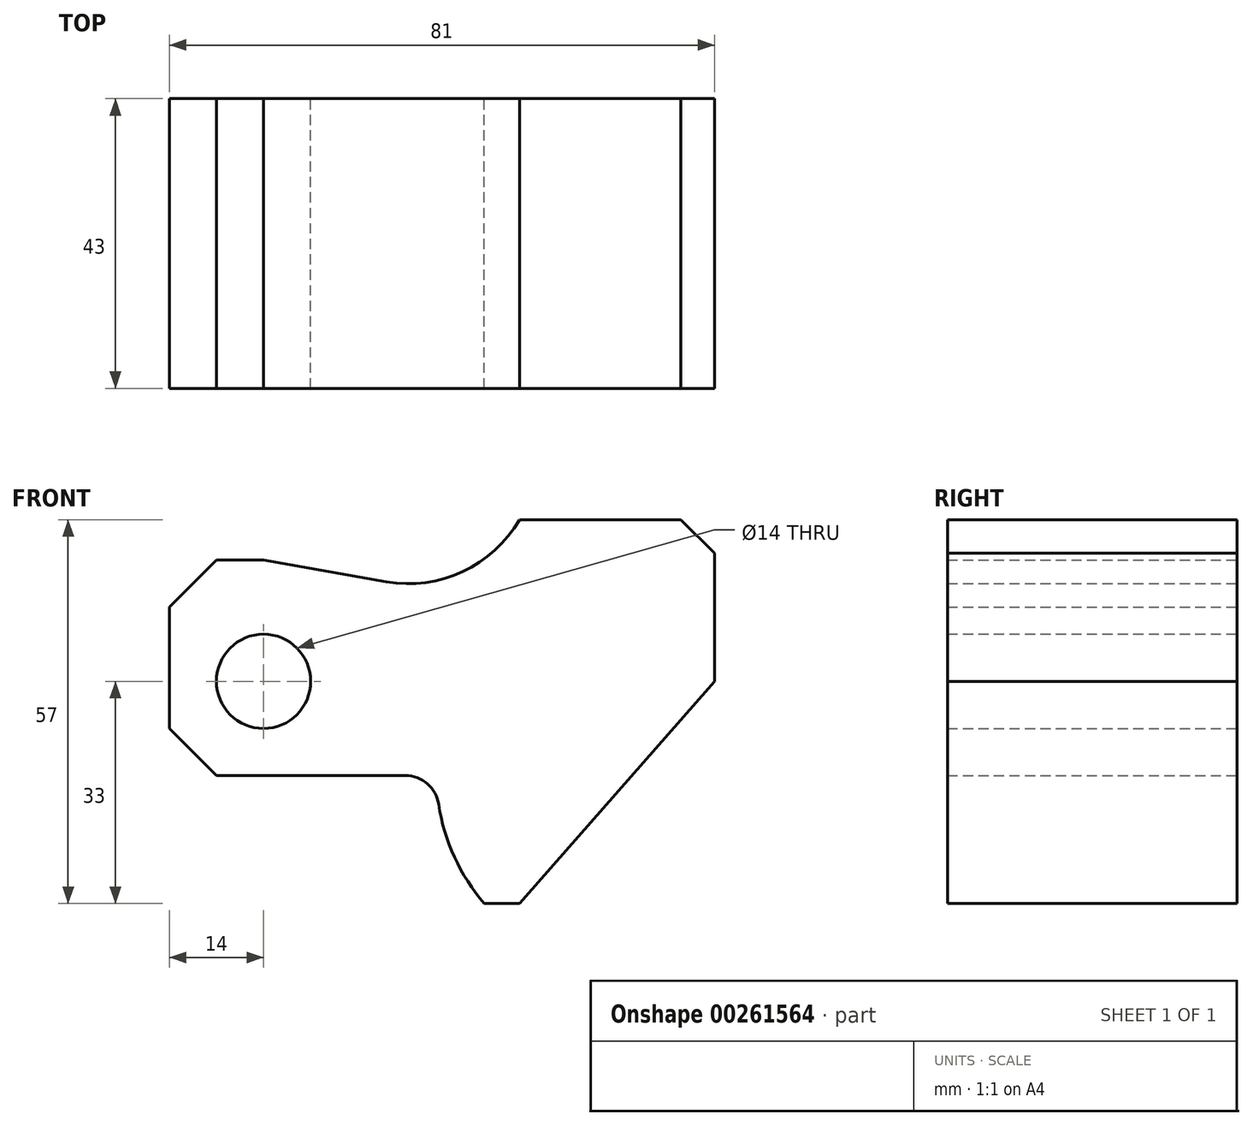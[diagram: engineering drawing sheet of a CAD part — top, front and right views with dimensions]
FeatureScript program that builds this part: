
annotation { "Feature Type Name" : "Feature", "Feature Type Description" : "" }
export const myFeature = defineFeature(function(context is Context, id is Id, definition is map)
    precondition{}
    {
        {
            var Q0;
            Q0=qCreatedBy(makeId("Front.planeOp"),FACE);
            var sketch = newSketch(context, id + "F0", { "sketchPlane" : qUnion([Q0])});
            skCircle(sketch, "E0", {"center": v(0, 0) * mm, "radius": 7 * mm});
            skLineSegment(sketch, "E1", {"start": v(-7, -14) * mm, "end": v(21.07, -14) * mm});
            skLineSegment(sketch, "E2", {"start": v(-7, -14) * mm, "end": v(-14, -7) * mm});
            skLineSegment(sketch, "E3", {"start": v(-14, -7) * mm, "end": v(-14, 11) * mm});
            skLineSegment(sketch, "E4", {"start": v(-14, 11) * mm, "end": v(-7, 18) * mm});
            skLineSegment(sketch, "E5", {"start": v(-7, 18) * mm, "end": v(0, 18) * mm});
            skLineSegment(sketch, "E6", {"start": v(0, 18) * mm, "end": v(18.24, 14.78) * mm});
            skLineSegment(sketch, "E7", {"start": v(67, 0) * mm, "end": v(67, 19) * mm});
            skLineSegment(sketch, "E8", {"start": v(32.79, -33) * mm, "end": v(38, -33) * mm});
            skLineSegment(sketch, "E9", {"start": v(38, -33) * mm, "end": v(67, 0) * mm});
            skLineSegment(sketch, "E10", {"start": v(67, 19) * mm, "end": v(62, 24) * mm});
            skLineSegment(sketch, "E11", {"start": v(62, 24) * mm, "end": v(38, 24) * mm});
            skArc(sketch, "E12", {"start": v(18.24, 14.78) * mm, "mid": v(29.57, 16.28) * mm, "end": v(38, 24) * mm});
            skLineSegment(sketch, "E13", {"start": v(21.07, -14) * mm, "end": v(54.7, -14) * mm, "construction": true});
            skArc(sketch, "E14", {"start": v(26.01, -18.26) * mm, "mid": v(28.35, -26.12) * mm, "end": v(32.79, -33) * mm});
            skArc(sketch, "E15", {"start": v(26.01, -18.26) * mm, "mid": v(24.33, -15.21) * mm, "end": v(21.07, -14) * mm});
            skSolve(sketch);
        }
        {
            var Q0;
            Q0=makeQuery(id+"F0.imprint","IMPRINT",FACE,{"disambiguationData":[TD([[makeQuery(id+"F0.imprint","IMPRINT",EDGE,{"derivedFrom":sQuery(id+"F0.wireOp",EDGE,"E0")}),-1.0]])]});
            extrude(context, id + "F1", {"entities" : qUnion([Q0]), "depth" : 43 * mm});
        }
    });
